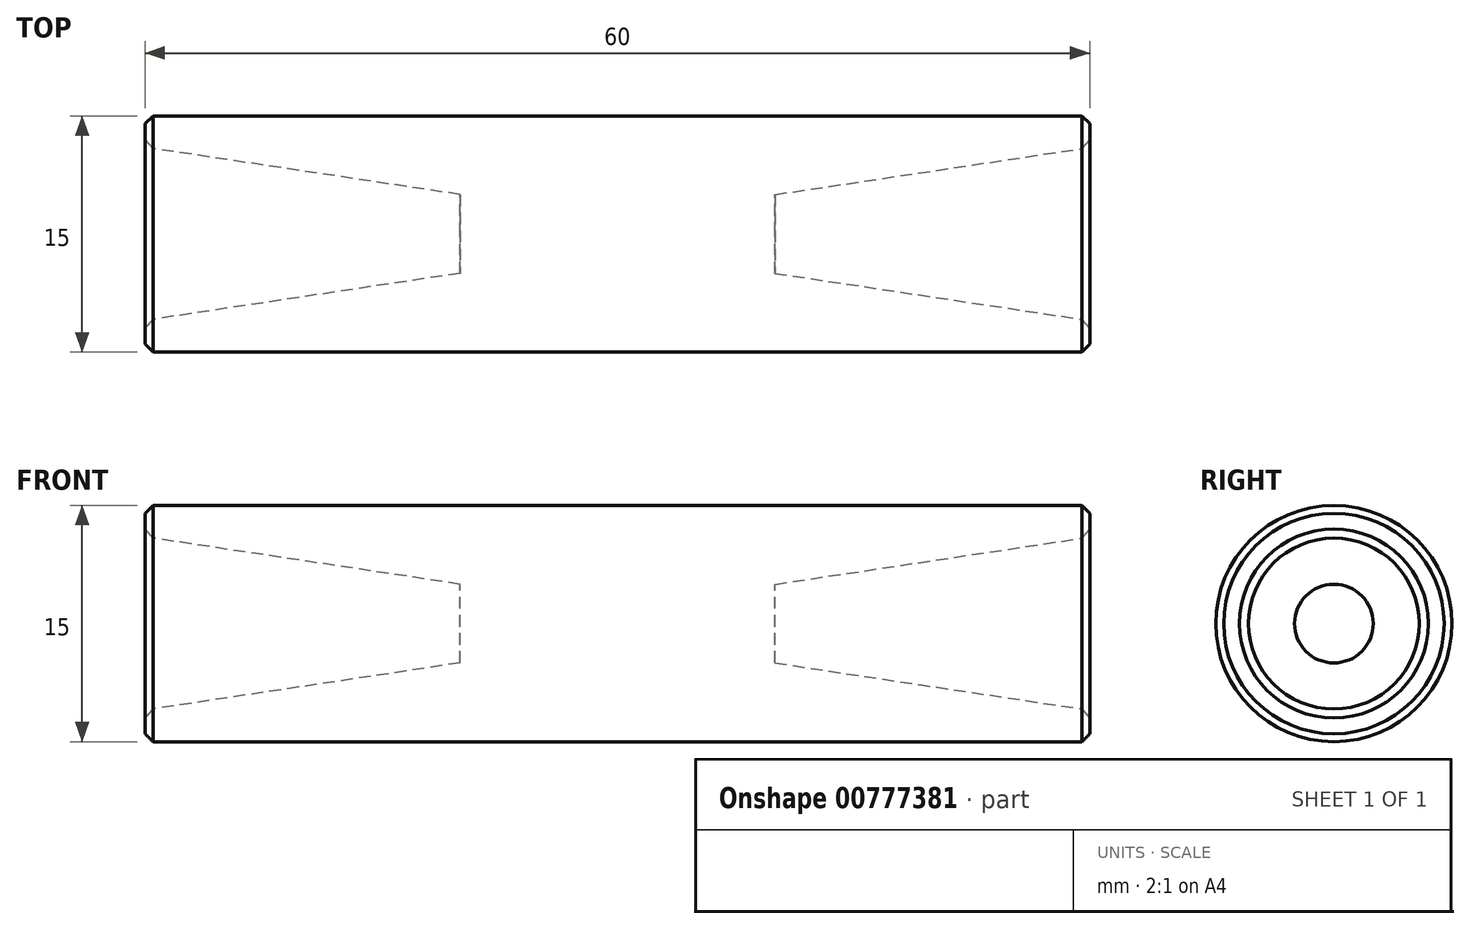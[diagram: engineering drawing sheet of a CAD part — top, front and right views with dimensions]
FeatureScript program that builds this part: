
annotation { "Feature Type Name" : "Feature", "Feature Type Description" : "" }
export const myFeature = defineFeature(function(context is Context, id is Id, definition is map)
    precondition{}
    {
        {
            var Q0;
            Q0=qCreatedBy(makeId("Front.planeOp"),FACE);
            var sketch = newSketch(context, id + "F0", { "sketchPlane" : qUnion([Q0])});
            skLineSegment(sketch, "E0", {"start": v(-30, 7.5) * mm, "end": v(0, 7.5) * mm});
            skLineSegment(sketch, "E1.bottom", {"start": v(0, 0) * mm, "end": v(-10, 0) * mm});
            skLineSegment(sketch, "E1.top", {"start": v(0, 2.5) * mm, "end": v(-10, 2.5) * mm});
            skLineSegment(sketch, "E1.left", {"start": v(0, 0) * mm, "end": v(0, 2.5) * mm, "construction": true});
            skLineSegment(sketch, "E1.right", {"start": v(-10, 0) * mm, "end": v(-10, 2.5) * mm});
            skLineSegment(sketch, "E2", {"start": v(-10, 2.5) * mm, "end": v(-30, 5.5) * mm});
            skLineSegment(sketch, "E3", {"start": v(-30, 5.5) * mm, "end": v(-30, 7.5) * mm});
            skLineSegment(sketch, "E4", {"start": v(0, 7.5) * mm, "end": v(0, 2.5) * mm, "construction": true});
            skLineSegment(sketch, "E5.MirrorCS", {"start": v(10, 0) * mm, "end": v(10, 2.5) * mm});
            skLineSegment(sketch, "E6.MirrorCS", {"start": v(30, 5.5) * mm, "end": v(30, 7.5) * mm});
            skLineSegment(sketch, "E7.MirrorCS", {"start": v(30, 7.5) * mm, "end": v(0, 7.5) * mm});
            skLineSegment(sketch, "E8.MirrorCS", {"start": v(0, 0) * mm, "end": v(10, 0) * mm});
            skLineSegment(sketch, "E9.MirrorCS", {"start": v(0, 2.5) * mm, "end": v(10, 2.5) * mm});
            skLineSegment(sketch, "E10.MirrorCS", {"start": v(10, 2.5) * mm, "end": v(30, 5.5) * mm});
            skSolve(sketch);
        }
        {
            var Q0;
            Q0 = qSketchRegion(id + "F0", true);
            var Q1;
            Q1=sQuery(id+"F0.wireOp",EDGE,"E1.bottom");
            revolve(context, id + "F1", {"surfaceOperationType" : NewSurfaceOperationType.NEW, "entities" : qUnion([Q0]), "axis" : qUnion([Q1]), "revolveType" : RevolveType.FULL});
        }
        {
            var Q0;
            Q0=makeQuery(id+"F1.opRevolve","SWEPT_EDGE",EDGE,{"disambiguationData":[OSD([sQuery(id+"F0.wireOp",EDGE,"E2"),sQuery(id+"F0.wireOp",EDGE,"E3")])]});
            var Q1;
            Q1=makeQuery(id+"F1.opRevolve","SWEPT_EDGE",EDGE,{"disambiguationData":[OSD([sQuery(id+"F0.wireOp",EDGE,"E0"),sQuery(id+"F0.wireOp",EDGE,"E3")])]});
            var Q2;
            Q2=makeQuery(id+"F1.opRevolve","SWEPT_EDGE",EDGE,{"disambiguationData":[OSD([sQuery(id+"F0.wireOp",EDGE,"E6.MirrorCS"),sQuery(id+"F0.wireOp",EDGE,"E10.MirrorCS")])]});
            var Q3;
            Q3=makeQuery(id+"F1.opRevolve","SWEPT_EDGE",EDGE,{"disambiguationData":[OSD([sQuery(id+"F0.wireOp",EDGE,"E6.MirrorCS"),sQuery(id+"F0.wireOp",EDGE,"E7.MirrorCS")])]});
            chamfer(context, id + "F2", {"entities" : qUnion([Q0, Q1, Q2, Q3]), "width" : .5 * mm, "tangentPropagation" : true});
        }
    });
